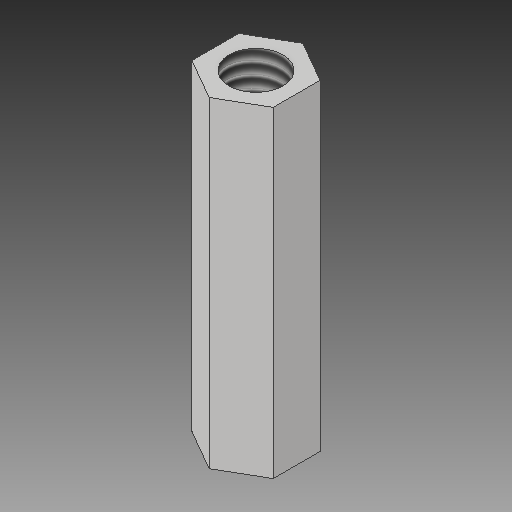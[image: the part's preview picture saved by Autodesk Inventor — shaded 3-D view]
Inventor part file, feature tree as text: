
AUTODESK INVENTOR PART (.ipt)
format: ipt  version: 2018 (Build 220112000, 112)  size: 109,056 bytes
history: native  units: mm
features: hole x5, sketch x4, extrude x1
ambient origin geometry x8: Origin, YZ Plane, XZ Plane, XY Plane, X Axis, Y Axis, Z Axis, Center Point
bodies: Solid1 (feature_tree)
feature tree (10):
  extrude  "Extrusion1"  Depth=12.0mm TaperAngle=0.0deg
  hole  "Hole1"  [1 undecoded]
  hole  "Hole3"  [1 undecoded]
  hole  "Hole5"  [1 undecoded]
  sketch  "Sketch1"  dims[d0=1.75mm d1=12.0mm d2=0.0mm]
  sketch  "Sketch2"  dims[d3=2.013mm d4=12.0mm d5=4.0mm d6=2.0mm d7=90.0deg d8=7.6mm d9=20.594885mm]
  sketch  "Sketch3"  dims[d10=2.013mm d11=4.52mm d12=4.0mm d13=2.0mm d14=90.0deg d15=5.77mm d16=120.0deg]
  hole  "Hole2"  [1 undecoded]
  sketch  "Sketch4"  dims[d17=2.013mm d18=6.202mm d19=4.0mm d20=2.0mm d21=90.0deg d22=7.452mm d23=120.0deg]
  hole  "Hole4"  [1 undecoded]
note: 5 required parameter values undecoded (feature->parameter linkage not recoverable at this tier; creation-order binding heuristic only, values carry confidence <= 0.55)
